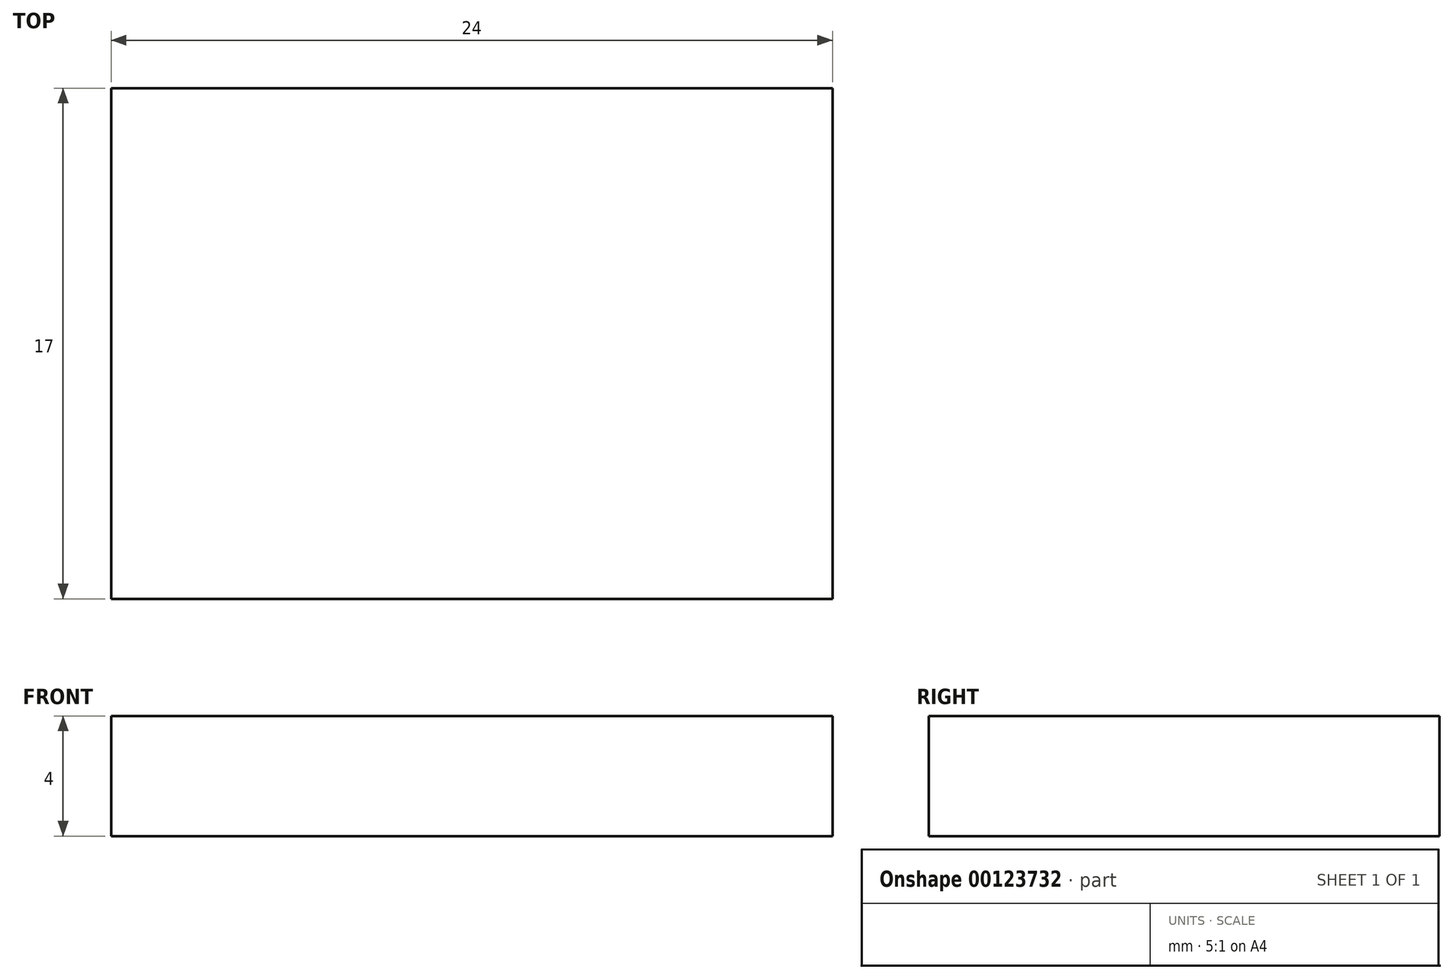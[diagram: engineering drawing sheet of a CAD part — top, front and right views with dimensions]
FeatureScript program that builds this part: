
annotation { "Feature Type Name" : "Feature", "Feature Type Description" : "" }
export const myFeature = defineFeature(function(context is Context, id is Id, definition is map)
    precondition{}
    {
        {
            var Q0;
            Q0=qCreatedBy(makeId("Top.planeOp"),FACE);
            var sketch = newSketch(context, id + "F0", { "sketchPlane" : qUnion([Q0])});
            skLineSegment(sketch, "E0.bottom", {"start": v(0, 17) * mm, "end": v(24, 17) * mm});
            skLineSegment(sketch, "E0.top", {"start": v(0, 0) * mm, "end": v(24, 0) * mm});
            skLineSegment(sketch, "E0.left", {"start": v(0, 17) * mm, "end": v(0, 0) * mm});
            skLineSegment(sketch, "E0.right", {"start": v(24, 17) * mm, "end": v(24, 0) * mm});
            skSolve(sketch);
        }
        {
            var Q0;
            Q0=qSketchRegion(id+"F0",true);
            extrude(context, id + "F1", {"entities" : qUnion([Q0]), "depth" : 4 * mm});
        }
    });
